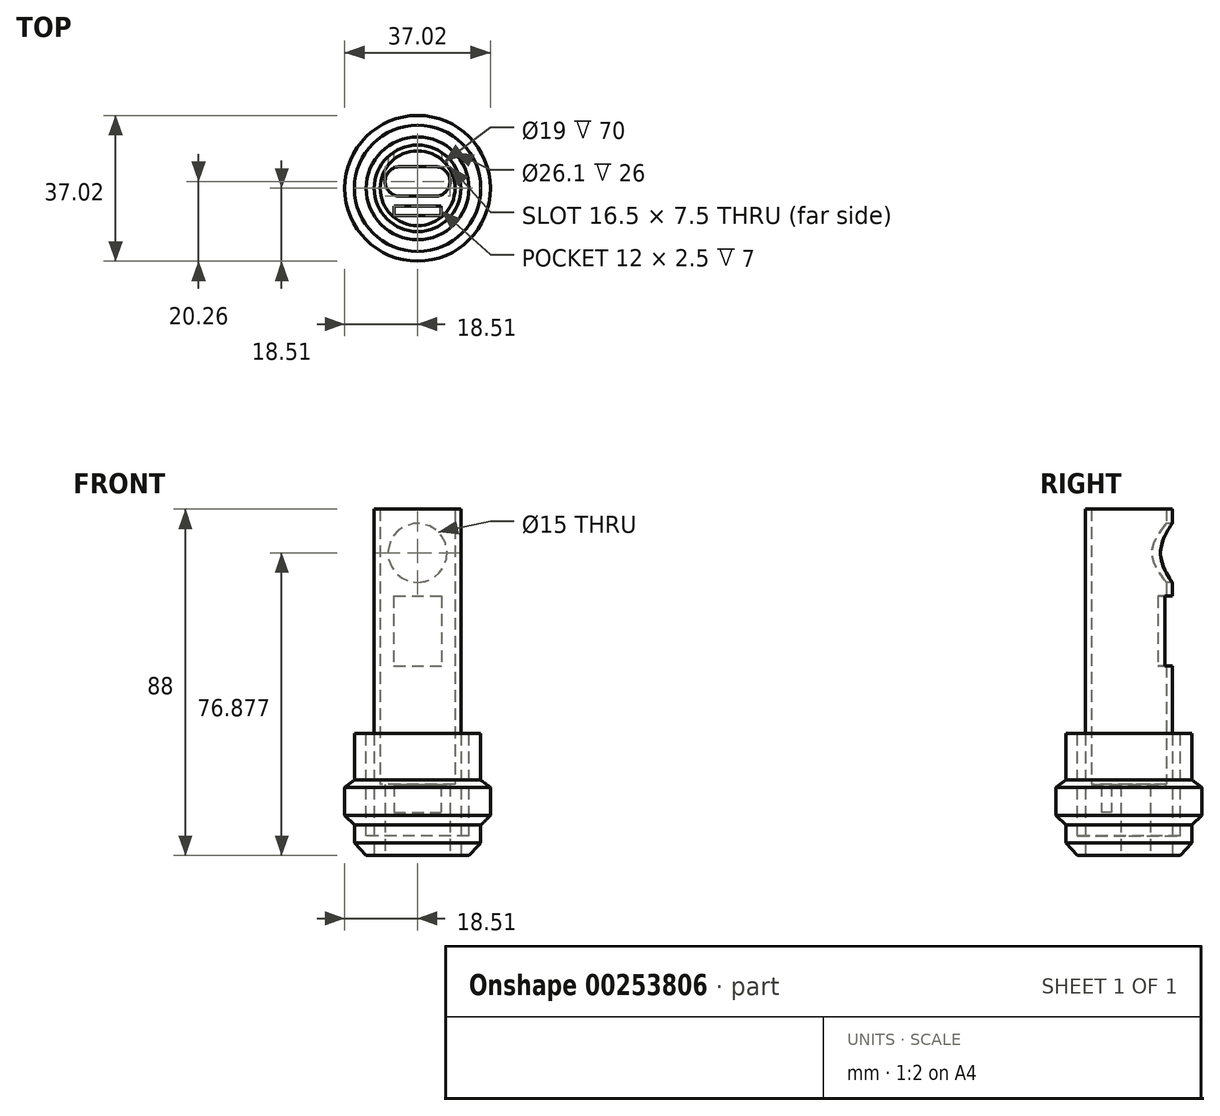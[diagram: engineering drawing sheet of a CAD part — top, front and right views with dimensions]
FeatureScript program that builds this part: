
annotation { "Feature Type Name" : "Feature", "Feature Type Description" : "" }
export const myFeature = defineFeature(function(context is Context, id is Id, definition is map)
    precondition{}
    {
        {
            var Q0;
            Q0=qCreatedBy(makeId("Front.planeOp"),FACE);
            var sketch = newSketch(context, id + "F0", { "sketchPlane" : qUnion([Q0])});
            skLineSegment(sketch, "E0", {"start": v(0, 0) * mm, "end": v(16.05, 0) * mm});
            skLineSegment(sketch, "E1", {"start": v(16.05, 0) * mm, "end": v(16.05, 31) * mm});
            skLineSegment(sketch, "E2", {"start": v(16.05, 31) * mm, "end": v(13.05, 31) * mm});
            skLineSegment(sketch, "E3", {"start": v(13.05, 31) * mm, "end": v(13.05, 5) * mm});
            skLineSegment(sketch, "E4", {"start": v(13.05, 5) * mm, "end": v(0, 5) * mm});
            skLineSegment(sketch, "E5", {"start": v(0, 5) * mm, "end": v(0, 0) * mm});
            skLineSegment(sketch, "E6", {"start": v(16.05, 3.15) * mm, "end": v(13.05, 0) * mm});
            skLineSegment(sketch, "E7", {"start": v(16.05, 7.74) * mm, "end": v(18.51, 10.18) * mm});
            skLineSegment(sketch, "E8", {"start": v(18.51, 10.18) * mm, "end": v(18.51, 17.3) * mm});
            skLineSegment(sketch, "E9", {"start": v(18.51, 17.3) * mm, "end": v(16.05, 19.15) * mm});
            skSolve(sketch);
        }
        {
            var Q0;
            {var subQ0=sQuery(id+"F0.wireOp",EDGE,"E2");Q0=makeQuery(id+"F0.imprint","IMPRINT",FACE,{"disambiguationData":[TD([[makeQuery(id+"F0.imprint","IMPRINT",EDGE,{"derivedFrom":subQ0}),1.0]])]});}
            var Q1;
            {var subQ0=sQuery(id+"F0.wireOp",EDGE,"E7");Q1=makeQuery(id+"F0.imprint","IMPRINT",FACE,{"disambiguationData":[TD([[makeQuery(id+"F0.imprint","IMPRINT",EDGE,{"derivedFrom":subQ0}),1.0]])]});}
            var Q2;
            Q2=sQuery(id+"F0.wireOp",EDGE,"E5");
            revolve(context, id + "F1", {"entities" : qUnion([Q0, Q1]), "axis" : qUnion([Q2]), "revolveType" : RevolveType.FULL});
        }
        {
            var Q0;
            Q0=qCreatedBy(makeId("Top.planeOp"),FACE);
            var sketch = newSketch(context, id + "F2", { "sketchPlane" : qUnion([Q0])});
            skCircle(sketch, "E10", {"center": v(0, 0) * mm, "radius": 11 * mm});
            skLineSegment(sketch, "E11.bottom", {"start": v(-4.5, 5.5) * mm, "end": v(4.5, 5.5) * mm});
            skLineSegment(sketch, "E11.top", {"start": v(-4.5, -2) * mm, "end": v(4.5, -2) * mm});
            skLineSegment(sketch, "E11.left", {"start": v(-8.25, 1.75) * mm, "end": v(-8.25, 1.75) * mm});
            skLineSegment(sketch, "E11.right", {"start": v(8.25, 1.75) * mm, "end": v(8.25, 1.75) * mm});
            skPoint(sketch, "E12.visualSharp", {"position": v(-8.25, 5.5) * mm});
            skArc(sketch, "E12.filletArc", {"start": v(-4.5, 5.5) * mm, "mid": v(-7.15, 4.4) * mm, "end": v(-8.25, 1.75) * mm});
            skPoint(sketch, "E13.visualSharp", {"position": v(-8.25, -2) * mm});
            skArc(sketch, "E13.filletArc", {"start": v(-8.25, 1.75) * mm, "mid": v(-7.15, -0.9) * mm, "end": v(-4.5, -2) * mm});
            skPoint(sketch, "E14.visualSharp", {"position": v(8.25, -2) * mm});
            skArc(sketch, "E14.filletArc", {"start": v(4.5, -2) * mm, "mid": v(7.15, -0.9) * mm, "end": v(8.25, 1.75) * mm});
            skPoint(sketch, "E15.visualSharp", {"position": v(8.25, 5.5) * mm});
            skArc(sketch, "E15.filletArc", {"start": v(8.25, 1.75) * mm, "mid": v(7.15, 4.4) * mm, "end": v(4.5, 5.5) * mm});
            skSolve(sketch);
        }
        {
            var Q0;
            Q0=makeQuery(id+"F2.imprint","IMPRINT",FACE,{"disambiguationData":[TD([[makeQuery(id+"F2.imprint","IMPRINT",EDGE,{"derivedFrom":sQuery(id+"F2.wireOp",EDGE,"E10")}),1.0]])]});
            extrude(context, id + "F3", {"entities" : qUnion([Q0]), "depth" : 11 * mm});
        }
        {
            var Q0;
            Q0=makeQuery(id+"F3.opExtrude","CAP_FACE",FACE,{"disambiguationData":[OSD([sQuery(id+"F2.wireOp",EDGE,"E10"),sQuery(id+"F2.wireOp",EDGE,"E11.bottom"),sQuery(id+"F2.wireOp",EDGE,"E11.top"),sQuery(id+"F2.wireOp",EDGE,"E12.filletArc"),sQuery(id+"F2.wireOp",EDGE,"E13.filletArc"),sQuery(id+"F2.wireOp",EDGE,"E14.filletArc"),sQuery(id+"F2.wireOp",EDGE,"E15.filletArc")])],"isStart":false});
            var sketch = newSketch(context, id + "F4", { "sketchPlane" : qUnion([Q0])});
            skLineSegment(sketch, "E16.bottom", {"start": v(-6, -4.47) * mm, "end": v(6, -4.47) * mm});
            skLineSegment(sketch, "E16.top", {"start": v(-6, -6.97) * mm, "end": v(6, -6.97) * mm});
            skLineSegment(sketch, "E16.left", {"start": v(-6, -4.47) * mm, "end": v(-6, -6.97) * mm});
            skLineSegment(sketch, "E16.right", {"start": v(6, -4.47) * mm, "end": v(6, -6.97) * mm});
            skSolve(sketch);
        }
        {
            var Q0;
            Q0=makeQuery(id+"F4.imprint","IMPRINT",FACE,{"disambiguationData":[TD([[makeQuery(id+"F4.imprint","IMPRINT",EDGE,{"derivedFrom":sQuery(id+"F4.wireOp",EDGE,"E16.bottom")}),1.0]])]});
            extrude(context, id + "F5", {"entities" : qUnion([Q0]), "operationType" : NewBodyOperationType.ADD, "depth" : 7 * mm});
        }
        {
            var Q0;
            Q0=makeQuery(id+"F5.opExtrude","CAP_FACE",FACE,{"disambiguationData":[OSD([sQuery(id+"F2.wireOp",EDGE,"E10"),sQuery(id+"F2.wireOp",EDGE,"E11.bottom"),sQuery(id+"F2.wireOp",EDGE,"E11.top"),sQuery(id+"F2.wireOp",EDGE,"E12.filletArc"),sQuery(id+"F2.wireOp",EDGE,"E13.filletArc"),sQuery(id+"F2.wireOp",EDGE,"E14.filletArc"),sQuery(id+"F2.wireOp",EDGE,"E15.filletArc"),sQuery(id+"F4.wireOp",EDGE,"E16.bottom"),sQuery(id+"F4.wireOp",EDGE,"E16.top"),sQuery(id+"F4.wireOp",EDGE,"E16.left"),sQuery(id+"F4.wireOp",EDGE,"E16.right")])],"isStart":false});
            var sketch = newSketch(context, id + "F6", { "sketchPlane" : qUnion([Q0])});
            skCircle(sketch, "E17.0", {"center": v(0, 0) * mm, "radius": 9.5 * mm});
            skSolve(sketch);
        }
        {
            var Q0;
            Q0=makeQuery(id+"F6.imprint","IMPRINT",FACE,{"disambiguationData":[TD([[makeQuery(id+"F6.imprint","IMPRINT",EDGE,{"derivedFrom":sQuery(id+"F6.wireOp",EDGE,"E17.0")}),-1.0]])]});
            extrude(context, id + "F7", {"entities" : qUnion([Q0]), "operationType" : NewBodyOperationType.ADD, "depth" : 70 * mm});
        }
        {
            var Q0;
            Q0=qCreatedBy(makeId("Front.planeOp"),FACE);
            var sketch = newSketch(context, id + "F8", { "sketchPlane" : qUnion([Q0])});
            skLineSegment(sketch, "E18.0", {"start": v(-11, 88) * mm, "end": v(11, 88) * mm});
            skCircle(sketch, "E19", {"center": v(0, 76.88) * mm, "radius": 7.5 * mm});
            skLineSegment(sketch, "E20.bottom", {"start": v(-6.05, 65.92) * mm, "end": v(6.05, 65.92) * mm});
            skLineSegment(sketch, "E20.top", {"start": v(-6.05, 48.17) * mm, "end": v(6.05, 48.17) * mm});
            skLineSegment(sketch, "E20.left", {"start": v(-6.05, 65.92) * mm, "end": v(-6.05, 48.17) * mm});
            skLineSegment(sketch, "E20.right", {"start": v(6.05, 65.92) * mm, "end": v(6.05, 48.17) * mm});
            skSolve(sketch);
        }
        {
            var Q0;
            Q0=makeQuery(id+"F8.imprint","IMPRINT",FACE,{"disambiguationData":[TD([[makeQuery(id+"F8.imprint","IMPRINT",EDGE,{"derivedFrom":sQuery(id+"F8.wireOp",EDGE,"E19")}),1.0]])]});
            var Q1;
            Q1=makeQuery(id+"F8.imprint","IMPRINT",FACE,{"disambiguationData":[TD([[makeQuery(id+"F8.imprint","IMPRINT",EDGE,{"derivedFrom":sQuery(id+"F8.wireOp",EDGE,"E20.bottom")}),-1.0]])]});
            extrude(context, id + "F9", {"entities" : qUnion([Q0, Q1]), "operationType" : NewBodyOperationType.REMOVE, "oppositeDirection" : true, "depth" : 25 * mm});
        }
    });
